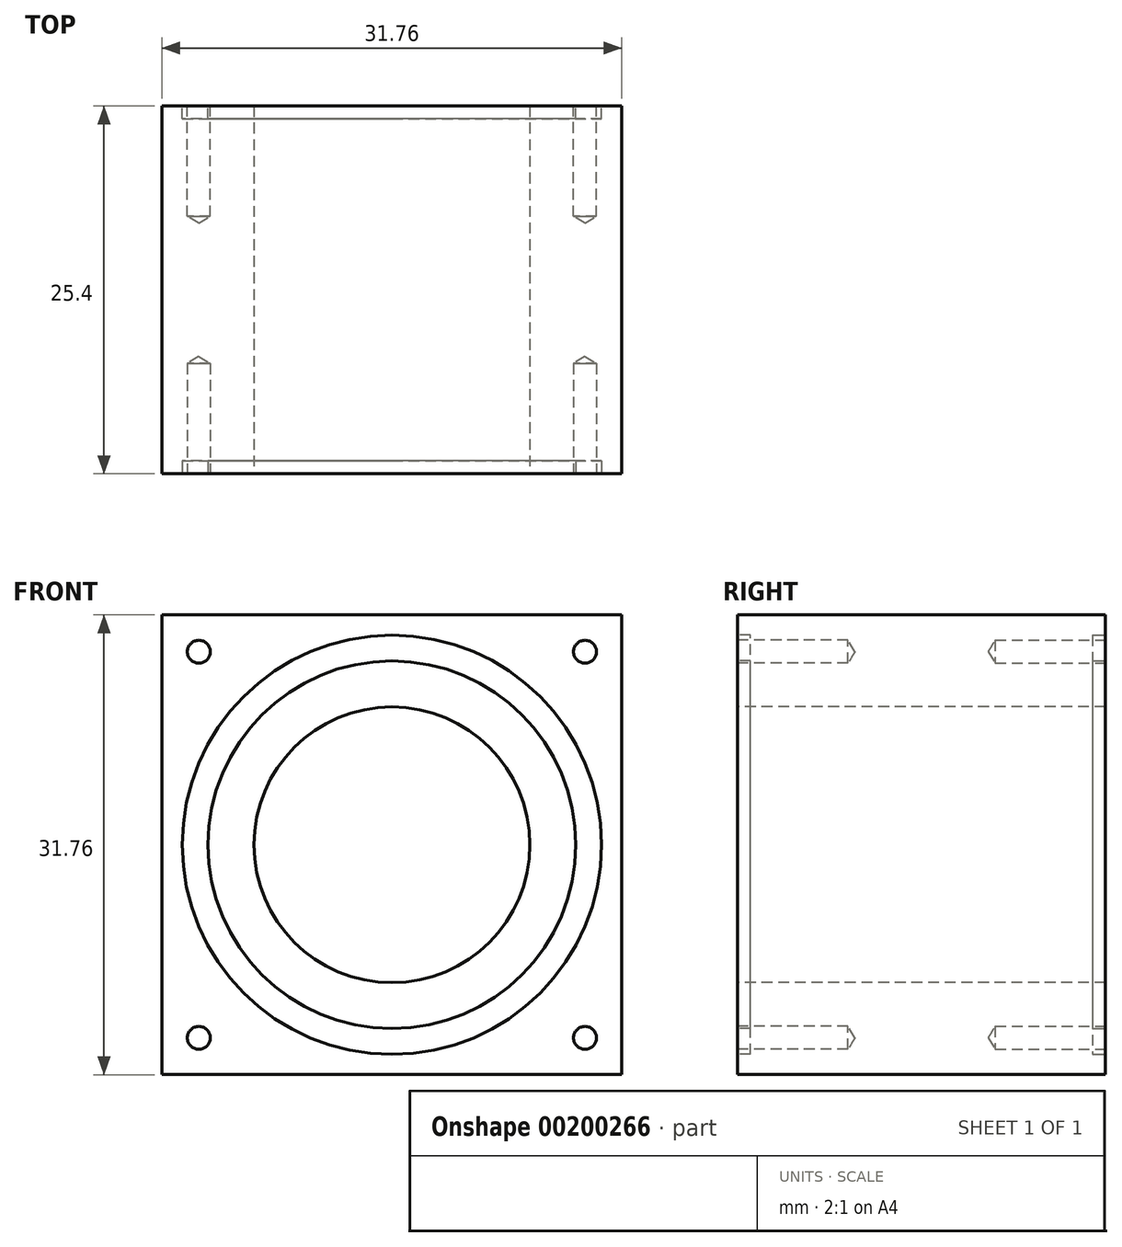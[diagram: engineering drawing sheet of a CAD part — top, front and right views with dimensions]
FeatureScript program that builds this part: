
annotation { "Feature Type Name" : "Feature", "Feature Type Description" : "" }
export const myFeature = defineFeature(function(context is Context, id is Id, definition is map)
    precondition{}
    {
        {
            var Q0;
            Q0=qCreatedBy(makeId("Front.planeOp"),FACE);
            var sketch = newSketch(context, id + "F0", { "sketchPlane" : qUnion([Q0])});
            skLineSegment(sketch, "E0.bottom", {"start": v(15.88, -15.87) * mm, "end": v(-15.88, -15.88) * mm});
            skLineSegment(sketch, "E0.top", {"start": v(15.88, 15.88) * mm, "end": v(-15.88, 15.87) * mm});
            skLineSegment(sketch, "E0.left", {"start": v(15.88, -15.88) * mm, "end": v(15.88, 15.88) * mm});
            skLineSegment(sketch, "E0.right", {"start": v(-15.88, -15.88) * mm, "end": v(-15.88, 15.88) * mm});
            skPoint(sketch, "E0.middle", {"position": v(0, 0) * mm});
            skSolve(sketch);
        }
        {
            var Q0;
            Q0=makeQuery(id+"F0.imprint","IMPRINT",FACE,{"disambiguationData":[TD([[makeQuery(id+"F0.imprint","IMPRINT",EDGE,{"derivedFrom":sQuery(id+"F0.wireOp",EDGE,"E0.bottom")}),-1.0]])]});
            extrude(context, id + "F1", {"entities" : qUnion([Q0]), "endBound" : BoundingType.SYMMETRIC, "depth" : 25.4 * mm});
        }
        {
            var Q0;
            Q0=makeQuery(id+"F1.opExtrude","CAP_FACE",FACE,{"disambiguationData":[OSD([sQuery(id+"F0.wireOp",EDGE,"E0.bottom"),sQuery(id+"F0.wireOp",EDGE,"E0.top"),sQuery(id+"F0.wireOp",EDGE,"E0.left"),sQuery(id+"F0.wireOp",EDGE,"E0.right")])],"isStart":false});
            var sketch = newSketch(context, id + "F2", { "sketchPlane" : qUnion([Q0])});
            skCircle(sketch, "E1", {"center": v(0, 0) * mm, "radius": 9.53 * mm});
            skSolve(sketch);
        }
        {
            var Q0;
            Q0=sQuery(id+"F2.wireOp",VERTEX,"E1.center");
            var Q1;
            Q1=makeQuery(id+"F1.opExtrude","SWEPT_BODY",BODY,{"disambiguationData":[OSD([sQuery(id+"F0.wireOp",EDGE,"E0.bottom"),sQuery(id+"F0.wireOp",EDGE,"E0.top"),sQuery(id+"F0.wireOp",EDGE,"E0.left"),sQuery(id+"F0.wireOp",EDGE,"E0.right")])]});
            hole(context, id + "F3", {"style" : HoleStyle.SIMPLE, "endStyle" : HoleEndStyle.THROUGH, "holeDiameter" : 19.05 * mm, "majorDiameter" : 6.35 * mm, "locations" : qUnion([Q0]), "scope" : qUnion([Q1]), "isTappedThrough" : true, "tappedDepth" : 12.7 * mm, "tapClearance" : 3});
        }
        {
            var Q0;
            Q0=makeQuery(id+"F1.opExtrude","CAP_FACE",FACE,{"disambiguationData":[OSD([sQuery(id+"F0.wireOp",EDGE,"E0.bottom"),sQuery(id+"F0.wireOp",EDGE,"E0.top"),sQuery(id+"F0.wireOp",EDGE,"E0.left"),sQuery(id+"F0.wireOp",EDGE,"E0.right")])],"isStart":false});
            var sketch = newSketch(context, id + "F4", { "sketchPlane" : qUnion([Q0])});
            skCircle(sketch, "E2", {"center": v(0, 0) * mm, "radius": 12.7 * mm});
            skCircle(sketch, "E3", {"center": v(0, 0) * mm, "radius": 14.48 * mm});
            skSolve(sketch);
        }
        {
            var Q0;
            Q0=makeQuery(id+"F4.imprint","IMPRINT",FACE,{"disambiguationData":[TD([[makeQuery(id+"F4.imprint","IMPRINT",EDGE,{"derivedFrom":sQuery(id+"F4.wireOp",EDGE,"E2")}),-1.0]])]});
            extrude(context, id + "F5", {"entities" : qUnion([Q0]), "operationType" : NewBodyOperationType.REMOVE, "oppositeDirection" : true, "depth" : 0.89 * mm});
        }
        {
            var Q0;
            Q0=makeQuery(id+"F1.opExtrude","CAP_FACE",FACE,{"disambiguationData":[OSD([sQuery(id+"F0.wireOp",EDGE,"E0.bottom"),sQuery(id+"F0.wireOp",EDGE,"E0.top"),sQuery(id+"F0.wireOp",EDGE,"E0.left"),sQuery(id+"F0.wireOp",EDGE,"E0.right")])],"isStart":true});
            var sketch = newSketch(context, id + "F6", { "sketchPlane" : qUnion([Q0])});
            skCircle(sketch, "E4", {"center": v(0, 0) * mm, "radius": 12.7 * mm});
            skCircle(sketch, "E5", {"center": v(0, 0) * mm, "radius": 14.48 * mm});
            skSolve(sketch);
        }
        {
            var Q0;
            Q0=makeQuery(id+"F6.imprint","IMPRINT",FACE,{"disambiguationData":[TD([[makeQuery(id+"F6.imprint","IMPRINT",EDGE,{"derivedFrom":sQuery(id+"F6.wireOp",EDGE,"E4")}),-1.0]])]});
            extrude(context, id + "F7", {"entities" : qUnion([Q0]), "operationType" : NewBodyOperationType.REMOVE, "oppositeDirection" : true, "depth" : 0.89 * mm});
        }
        {
            var Q0;
            {var subQ0=sQuery(id+"F0.wireOp",EDGE,"E0.right");var subQ1=sQuery(id+"F0.wireOp",EDGE,"E0.left");var subQ2=sQuery(id+"F0.wireOp",EDGE,"E0.top");var subQ3=sQuery(id+"F0.wireOp",EDGE,"E0.bottom");Q0=makeQuery(id+"F7.boolean.opBoolean","SPLIT",FACE,{"disambiguationData":[TD([makeQuery(id+"F1.opExtrude","SWEPT_FACE",FACE,{"disambiguationData":[OSD([subQ3])]})])],"derivedFrom":makeQuery(id+"F1.opExtrude","CAP_FACE",FACE,{"disambiguationData":[OSD([subQ3,subQ2,subQ1,subQ0])],"isStart":true})});}
            var sketch = newSketch(context, id + "F8", { "sketchPlane" : qUnion([Q0])});
            skLineSegment(sketch, "E6.bottom", {"start": v(-13.33, 13.34) * mm, "end": v(13.34, 13.34) * mm});
            skLineSegment(sketch, "E6.top", {"start": v(-13.34, -13.34) * mm, "end": v(13.33, -13.34) * mm});
            skLineSegment(sketch, "E6.left", {"start": v(-13.33, 13.34) * mm, "end": v(-13.34, -13.34) * mm});
            skLineSegment(sketch, "E6.right", {"start": v(13.34, 13.34) * mm, "end": v(13.33, -13.34) * mm});
            skPoint(sketch, "E6.middle", {"position": v(0, 0) * mm});
            skSolve(sketch);
        }
        {
            var Q0;
            Q0=sQuery(id+"F8.wireOp",VERTEX,"E6.left.start");
            var Q1;
            Q1=sQuery(id+"F8.wireOp",VERTEX,"E6.right.start");
            var Q2;
            Q2=sQuery(id+"F8.wireOp",VERTEX,"E6.right.end");
            var Q3;
            Q3=sQuery(id+"F8.wireOp",VERTEX,"E6.left.end");
            var Q4;
            Q4=makeQuery(id+"F1.opExtrude","SWEPT_BODY",BODY,{"disambiguationData":[OSD([sQuery(id+"F0.wireOp",EDGE,"E0.bottom"),sQuery(id+"F0.wireOp",EDGE,"E0.top"),sQuery(id+"F0.wireOp",EDGE,"E0.left"),sQuery(id+"F0.wireOp",EDGE,"E0.right")])]});
            hole(context, id + "F9", {"style" : HoleStyle.SIMPLE, "endStyle" : HoleEndStyle.BLIND, "holeDiameter" : 1.59 * mm, "holeDepth" : 7.62 * mm, "locations" : qUnion([Q0, Q1, Q2, Q3]), "scope" : qUnion([Q4])});
        }
        {
            var Q0;
            {var subQ0=sQuery(id+"F0.wireOp",EDGE,"E0.right");var subQ1=sQuery(id+"F0.wireOp",EDGE,"E0.left");var subQ2=sQuery(id+"F0.wireOp",EDGE,"E0.top");var subQ3=sQuery(id+"F0.wireOp",EDGE,"E0.bottom");Q0=makeQuery(id+"F5.boolean.opBoolean","SPLIT",FACE,{"disambiguationData":[TD([makeQuery(id+"F1.opExtrude","SWEPT_FACE",FACE,{"disambiguationData":[OSD([subQ3])]})])],"derivedFrom":makeQuery(id+"F1.opExtrude","CAP_FACE",FACE,{"disambiguationData":[OSD([subQ3,subQ2,subQ1,subQ0])],"isStart":false})});}
            var sketch = newSketch(context, id + "F10", { "sketchPlane" : qUnion([Q0])});
            skLineSegment(sketch, "E7.bottom", {"start": v(13.34, -13.33) * mm, "end": v(-13.33, -13.34) * mm});
            skLineSegment(sketch, "E7.top", {"start": v(13.34, 13.34) * mm, "end": v(-13.33, 13.34) * mm});
            skLineSegment(sketch, "E7.left", {"start": v(13.34, -13.33) * mm, "end": v(13.34, 13.34) * mm});
            skLineSegment(sketch, "E7.right", {"start": v(-13.33, -13.34) * mm, "end": v(-13.33, 13.34) * mm});
            skPoint(sketch, "E7.middle", {"position": v(0, 0) * mm});
            skSolve(sketch);
        }
        {
            var Q0;
            Q0=sQuery(id+"F10.wireOp",VERTEX,"E7.right.end");
            var Q1;
            Q1=sQuery(id+"F10.wireOp",VERTEX,"E7.left.end");
            var Q2;
            Q2=sQuery(id+"F10.wireOp",VERTEX,"E7.bottom.start");
            var Q3;
            Q3=sQuery(id+"F10.wireOp",VERTEX,"E7.right.start");
            var Q4;
            Q4=makeQuery(id+"F1.opExtrude","SWEPT_BODY",BODY,{"disambiguationData":[OSD([sQuery(id+"F0.wireOp",EDGE,"E0.bottom"),sQuery(id+"F0.wireOp",EDGE,"E0.top"),sQuery(id+"F0.wireOp",EDGE,"E0.left"),sQuery(id+"F0.wireOp",EDGE,"E0.right")])]});
            hole(context, id + "F11", {"style" : HoleStyle.SIMPLE, "endStyle" : HoleEndStyle.BLIND, "holeDiameter" : 1.59 * mm, "holeDepth" : 7.62 * mm, "locations" : qUnion([Q0, Q1, Q2, Q3]), "scope" : qUnion([Q4])});
        }
    });
